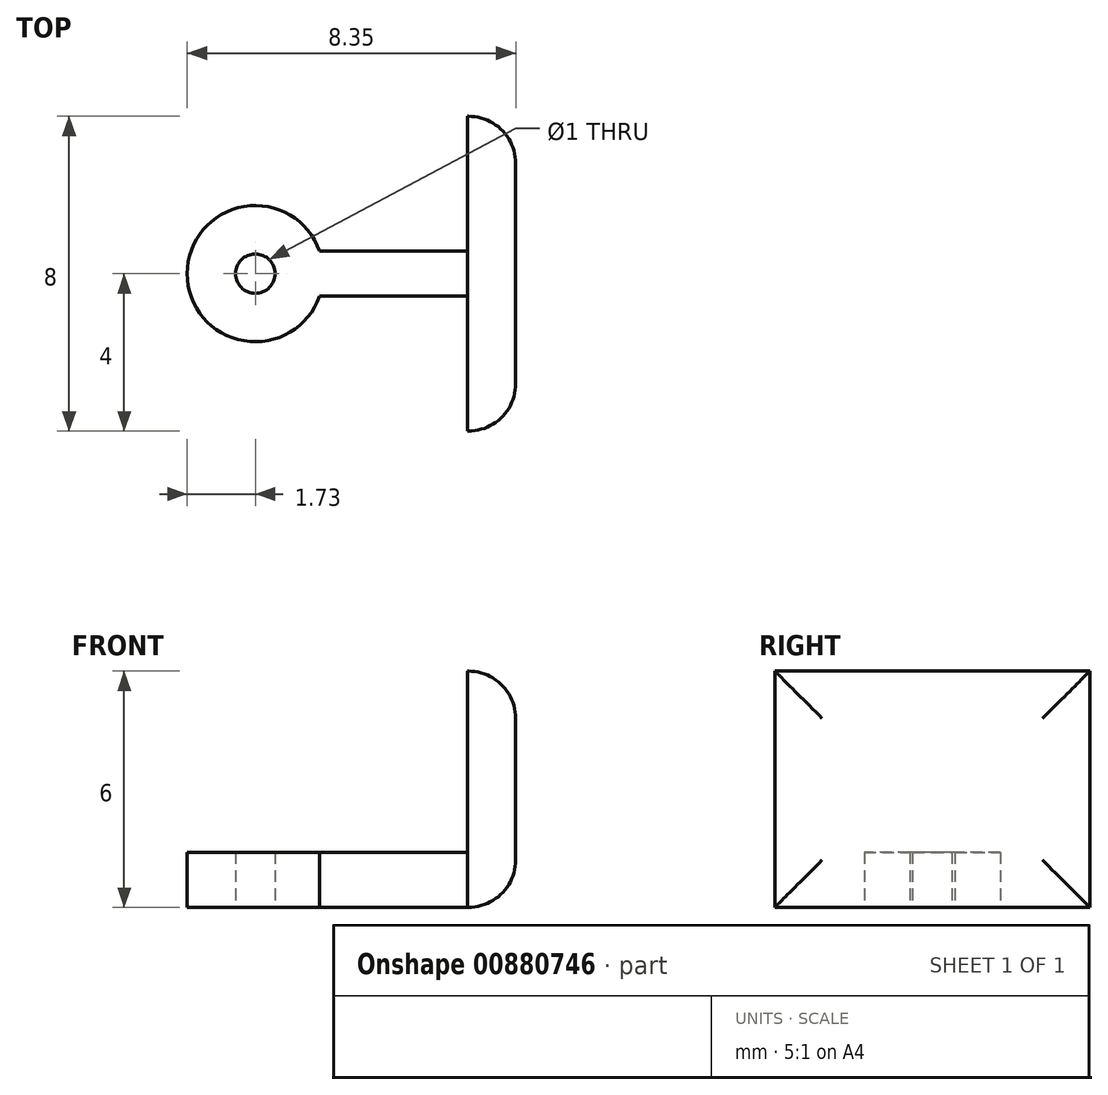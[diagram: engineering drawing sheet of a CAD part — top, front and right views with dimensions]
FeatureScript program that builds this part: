
annotation { "Feature Type Name" : "Feature", "Feature Type Description" : "" }
export const myFeature = defineFeature(function(context is Context, id is Id, definition is map)
    precondition{}
    {
        {
            var Q0;
            Q0=qCreatedBy(makeId("Top.planeOp"),FACE);
            var sketch = newSketch(context, id + "F0", { "sketchPlane" : qUnion([Q0])});
            skCircle(sketch, "E0", {"center": v(0, 0) * mm, "radius": 0.5 * mm});
            skCircle(sketch, "E1.0", {"center": v(0, 0) * mm, "radius": 1.73 * mm});
            skLineSegment(sketch, "E2.bottom", {"start": v(6, -0.57) * mm, "end": v(-6, -0.57) * mm});
            skLineSegment(sketch, "E2.top", {"start": v(6, 0.57) * mm, "end": v(-6, 0.57) * mm});
            skLineSegment(sketch, "E2.left", {"start": v(6, -0.57) * mm, "end": v(6, 0.57) * mm});
            skLineSegment(sketch, "E2.right", {"start": v(-6, -0.57) * mm, "end": v(-6, 0.57) * mm});
            skLineSegment(sketch, "E3.bottom", {"start": v(6.62, -4) * mm, "end": v(5.38, -4) * mm});
            skLineSegment(sketch, "E3.top", {"start": v(6.62, 4) * mm, "end": v(5.38, 4) * mm});
            skLineSegment(sketch, "E3.left", {"start": v(6.62, -4) * mm, "end": v(6.62, 4) * mm});
            skLineSegment(sketch, "E3.right", {"start": v(5.38, -4) * mm, "end": v(5.38, 4) * mm});
            skPoint(sketch, "E3.middle", {"position": v(6, 0) * mm});
            skSolve(sketch);
        }
        {
            var Q0;
            {var subQ0=sQuery(id+"F0.wireOp",EDGE,"E2.top");var subQ1=sQuery(id+"F0.wireOp",EDGE,"E1.0");var subQ2=makeQuery(id+"F0.imprint","INTERSECT",VERTEX,{"disambiguationData":[OD(0.0)],"derivedFrom":[subQ1,subQ0]});Q0=makeQuery(id+"F0.imprint","IMPRINT",FACE,{"disambiguationData":[TD([[makeQuery(id+"F0.imprint","IMPRINT",EDGE,{"disambiguationData":[TD([[subQ2,1.0]])],"derivedFrom":subQ1}),1.0]])]});}
            var Q1;
            {var subQ0=sQuery(id+"F0.wireOp",EDGE,"E2.bottom");var subQ1=sQuery(id+"F0.wireOp",EDGE,"E1.0");var subQ2=makeQuery(id+"F0.imprint","INTERSECT",VERTEX,{"disambiguationData":[OD(0.0)],"derivedFrom":[subQ1,subQ0]});Q1=makeQuery(id+"F0.imprint","IMPRINT",FACE,{"disambiguationData":[TD([[makeQuery(id+"F0.imprint","IMPRINT",EDGE,{"disambiguationData":[TD([[subQ2,-1.0]])],"derivedFrom":subQ1}),1.0]])]});}
            var Q2;
            {var subQ5=sQuery(id+"F0.wireOp",EDGE,"E2.left");Q2=makeQuery(id+"F0.imprint","IMPRINT",FACE,{"disambiguationData":[TD([[makeQuery(id+"F0.imprint","IMPRINT",EDGE,{"derivedFrom":subQ5}),1.0]])]});}
            var Q3;
            Q3=makeQuery(id+"F0.imprint","IMPRINT",FACE,{"disambiguationData":[TD([[makeQuery(id+"F0.imprint","IMPRINT",EDGE,{"derivedFrom":sQuery(id+"F0.wireOp",EDGE,"E0")}),-1.0]])]});
            var Q4;
            {var subQ0=sQuery(id+"F0.wireOp",EDGE,"E2.top");var subQ1=sQuery(id+"F0.wireOp",EDGE,"E1.0");var subQ2=makeQuery(id+"F0.imprint","INTERSECT",VERTEX,{"disambiguationData":[OD(1.0)],"derivedFrom":[subQ1,subQ0]});Q4=makeQuery(id+"F0.imprint","IMPRINT",FACE,{"disambiguationData":[TD([[makeQuery(id+"F0.imprint","IMPRINT",EDGE,{"disambiguationData":[TD([[subQ2,1.0]])],"derivedFrom":subQ1}),-1.0]])]});}
            extrude(context, id + "F1", {"entities" : qUnion([Q0, Q1, Q2, Q3, Q4]), "depth" : 1.4 * mm, "offsetDistance" : 25 * mm});
        }
        {
            var Q0;
            {var subQ0=sQuery(id+"F0.wireOp",EDGE,"E2.left");Q0=makeQuery(id+"F0.imprint","IMPRINT",FACE,{"disambiguationData":[TD([[makeQuery(id+"F0.imprint","IMPRINT",EDGE,{"derivedFrom":subQ0}),-1.0]])]});}
            var Q1;
            {var subQ0=sQuery(id+"F0.wireOp",EDGE,"E2.left");Q1=makeQuery(id+"F0.imprint","IMPRINT",FACE,{"disambiguationData":[TD([[makeQuery(id+"F0.imprint","IMPRINT",EDGE,{"derivedFrom":subQ0}),1.0]])]});}
            extrude(context, id + "F2", {"entities" : qUnion([Q0, Q1]), "operationType" : NewBodyOperationType.ADD, "depth" : 6 * mm, "offsetDistance" : 25 * mm});
        }
        {
            var Q0;
            Q0=makeQuery(id+"F2.opExtrude","SWEPT_EDGE",EDGE,{"disambiguationData":[OSD([sQuery(id+"F0.wireOp",EDGE,"E3.bottom"),sQuery(id+"F0.wireOp",EDGE,"E3.left")])]});
            var Q1;
            Q1=makeQuery(id+"F2.opExtrude","SWEPT_EDGE",EDGE,{"disambiguationData":[OSD([sQuery(id+"F0.wireOp",EDGE,"E3.top"),sQuery(id+"F0.wireOp",EDGE,"E3.left")])]});
            var Q2;
            Q2=makeQuery(id+"F2.opExtrude","CAP_EDGE",EDGE,{"disambiguationData":[OSD([sQuery(id+"F0.wireOp",EDGE,"E3.left")])],"isStart":false});
            var Q3;
            Q3=makeQuery(id+"F2.opExtrude","CAP_EDGE",EDGE,{"disambiguationData":[OSD([sQuery(id+"F0.wireOp",EDGE,"E3.left")])],"isStart":true});
            fillet(context, id + "F3", {"entities" : qUnion([Q0, Q1, Q2, Q3]), "radius" : 1.2 * mm, "tangentPropagation" : true, "allowEdgeOverflow" : false});
        }
    });
